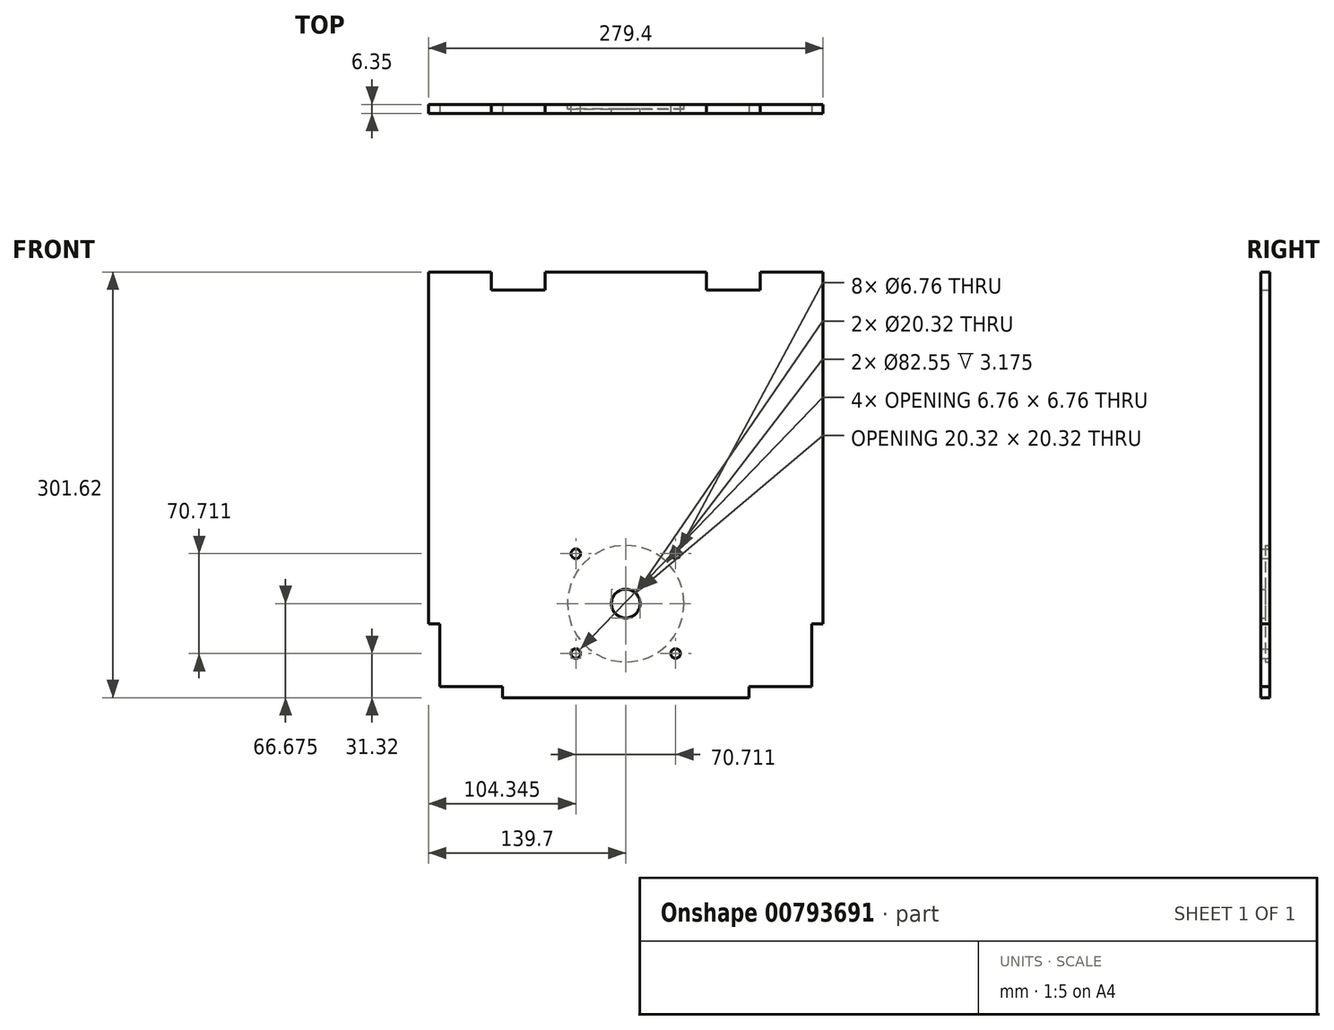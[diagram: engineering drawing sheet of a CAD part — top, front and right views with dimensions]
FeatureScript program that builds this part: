
annotation { "Feature Type Name" : "Feature", "Feature Type Description" : "" }
export const myFeature = defineFeature(function(context is Context, id is Id, definition is map)
    precondition{}
    {
        {
            var Q0;
            Q0=qCreatedBy(makeId("Front.planeOp"),FACE);
            var sketch = newSketch(context, id + "F0", { "sketchPlane" : qUnion([Q0])});
            skLineSegment(sketch, "E0.bottom", {"start": v(0, 0) * mm, "end": v(279.4, 0) * mm});
            skLineSegment(sketch, "E0.top", {"start": v(0, 301.63) * mm, "end": v(44.45, 301.63) * mm});
            skLineSegment(sketch, "E0.left", {"start": v(0, 0) * mm, "end": v(0, 301.63) * mm});
            skLineSegment(sketch, "E0.right", {"start": v(279.4, 0) * mm, "end": v(279.4, 301.63) * mm});
            skLineSegment(sketch, "E1", {"start": v(139.7, 0) * mm, "end": v(139.7, 301.63) * mm, "construction": true});
            skCircle(sketch, "E2", {"center": v(139.7, 66.68) * mm, "radius": 10.16 * mm});
            skCircle(sketch, "E3", {"center": v(139.7, 66.68) * mm, "radius": 50 * mm, "construction": true});
            skLineSegment(sketch, "E4.bottom", {"start": v(184.7, 21.68) * mm, "end": v(94.7, 21.68) * mm, "construction": true});
            skLineSegment(sketch, "E4.top", {"start": v(184.7, 111.67) * mm, "end": v(94.7, 111.67) * mm, "construction": true});
            skLineSegment(sketch, "E4.left", {"start": v(184.7, 21.68) * mm, "end": v(184.7, 111.67) * mm, "construction": true});
            skLineSegment(sketch, "E4.right", {"start": v(94.7, 21.68) * mm, "end": v(94.7, 111.67) * mm, "construction": true});
            skPoint(sketch, "E5", {"position": v(104.34, 31.32) * mm});
            skLineSegment(sketch, "E6", {"start": v(104.34, 31.32) * mm, "end": v(104.34, 21.68) * mm, "construction": true});
            skLineSegment(sketch, "E7", {"start": v(104.34, 31.32) * mm, "end": v(94.7, 31.32) * mm, "construction": true});
            skLineSegment(sketch, "E8", {"start": v(94.7, 66.68) * mm, "end": v(184.7, 66.68) * mm, "construction": true});
            skPoint(sketch, "E9.MirrorP", {"position": v(104.34, 102.03) * mm});
            skPoint(sketch, "E10.MirrorP", {"position": v(175.06, 31.32) * mm});
            skPoint(sketch, "E11.MirrorP", {"position": v(175.06, 102.03) * mm});
            skLineSegment(sketch, "E12.top", {"start": v(234.95, 288.93) * mm, "end": v(196.85, 288.93) * mm});
            skLineSegment(sketch, "E12.left", {"start": v(234.95, 288.93) * mm, "end": v(234.95, 301.63) * mm});
            skLineSegment(sketch, "E12.right", {"start": v(196.85, 288.93) * mm, "end": v(196.85, 301.63) * mm});
            skLineSegment(sketch, "E13.MirrorCS", {"start": v(82.55, 288.93) * mm, "end": v(82.55, 301.63) * mm});
            skLineSegment(sketch, "E14.MirrorCS", {"start": v(44.45, 288.93) * mm, "end": v(82.55, 288.93) * mm});
            skLineSegment(sketch, "E15.MirrorCS", {"start": v(44.45, 288.93) * mm, "end": v(44.45, 301.63) * mm});
            skLineSegment(sketch, "E16.trimOffspring", {"start": v(234.95, 301.63) * mm, "end": v(279.4, 301.63) * mm});
            skPoint(sketch, "E17.MirrorCS.end.orphan", {"position": v(82.55, 301.63) * mm});
            skPoint(sketch, "E17.MirrorCS.start.orphan", {"position": v(44.45, 301.63) * mm});
            skLineSegment(sketch, "E18.trimOffspring", {"start": v(82.55, 301.63) * mm, "end": v(196.85, 301.63) * mm});
            skSolve(sketch);
        }
        {
            var Q0;
            Q0 = qSketchRegion(id + "F0", true);
            extrude(context, id + "F1", {"entities" : qUnion([Q0]), "depth" : 6.35 * mm, "offsetDistance" : 25.4 * mm});
        }
        {
            var Q0;
            Q0=sQuery(id+"F0.wireOp",VERTEX,"E11.MirrorP");
            var Q1;
            Q1=sQuery(id+"F0.wireOp",VERTEX,"E9.MirrorP");
            var Q2;
            Q2=sQuery(id+"F0.wireOp",VERTEX,"E10.MirrorP");
            var Q3;
            Q3=sQuery(id+"F0.wireOp",VERTEX,"E5");
            var Q4;
            Q4=makeQuery(id+"F1.opExtrude","SWEPT_BODY",BODY,{"disambiguationData":[OSD([sQuery(id+"F0.wireOp",EDGE,"E0.bottom"),sQuery(id+"F0.wireOp",EDGE,"E0.top"),sQuery(id+"F0.wireOp",EDGE,"E0.left"),sQuery(id+"F0.wireOp",EDGE,"E0.right"),sQuery(id+"F0.wireOp",EDGE,"E2")])]});
            hole(context, id + "F2", {"style" : HoleStyle.SIMPLE, "endStyle" : HoleEndStyle.THROUGH, "oppositeDirection" : true, "standardTappedOrClearance" : lookupTablePath({ "fit" : "Normal (ASME)", "standard" : "ANSI", "size" : "1/4", "type" : "Clearance" }), "standardBlindInLast" : lookupTablePath({ "fit" : "Free", "standard" : "ANSI", "size" : "1/4", "type" : "Clearance" }), "holeDiameter" : 6.76 * mm, "majorDiameter" : 6.35 * mm, "isTappedThrough" : true, "tappedDepth" : 12.7 * mm, "tapClearance" : 3, "locations" : qUnion([Q0, Q1, Q2, Q3]), "scope" : qUnion([Q4])});
        }
        {
            var Q0;
            Q0=makeQuery(id+"F1.opExtrude","CAP_FACE",FACE,{"disambiguationData":[OSD([sQuery(id+"F0.wireOp",EDGE,"E0.bottom"),sQuery(id+"F0.wireOp",EDGE,"E0.top"),sQuery(id+"F0.wireOp",EDGE,"E0.left"),sQuery(id+"F0.wireOp",EDGE,"E0.right"),sQuery(id+"F0.wireOp",EDGE,"E2")])],"isStart":true});
            var sketch = newSketch(context, id + "F3", { "sketchPlane" : qUnion([Q0])});
            skCircle(sketch, "E19", {"center": v(-139.7, 66.68) * mm, "radius": 41.28 * mm});
            skSolve(sketch);
        }
        {
            var Q0;
            Q0 = qSketchRegion(id + "F3", true);
            extrude(context, id + "F4", {"entities" : qUnion([Q0]), "operationType" : NewBodyOperationType.REMOVE, "oppositeDirection" : true, "depth" : 3.17 * mm, "offsetDistance" : 25.4 * mm});
        }
        {
            var Q0;
            Q0=makeQuery(id+"F1.opExtrude","CAP_FACE",FACE,{"disambiguationData":[OSD([sQuery(id+"F0.wireOp",EDGE,"E0.bottom"),sQuery(id+"F0.wireOp",EDGE,"E0.top"),sQuery(id+"F0.wireOp",EDGE,"E0.left"),sQuery(id+"F0.wireOp",EDGE,"E0.right"),sQuery(id+"F0.wireOp",EDGE,"E2"),sQuery(id+"F0.wireOp",EDGE,"E12.top"),sQuery(id+"F0.wireOp",EDGE,"E12.left"),sQuery(id+"F0.wireOp",EDGE,"E12.right"),sQuery(id+"F0.wireOp",EDGE,"E13.MirrorCS"),sQuery(id+"F0.wireOp",EDGE,"E14.MirrorCS"),sQuery(id+"F0.wireOp",EDGE,"E15.MirrorCS"),sQuery(id+"F0.wireOp",EDGE,"E16.trimOffspring"),sQuery(id+"F0.wireOp",EDGE,"E18.trimOffspring")])],"isStart":false});
            var sketch = newSketch(context, id + "F5", { "sketchPlane" : qUnion([Q0])});
            skLineSegment(sketch, "E20", {"start": v(139.7, 301.63) * mm, "end": v(139.7, 0) * mm, "construction": true});
            skLineSegment(sketch, "E21", {"start": v(52.39, 0) * mm, "end": v(52.39, 7.94) * mm});
            skLineSegment(sketch, "E22", {"start": v(52.39, 7.94) * mm, "end": v(7.94, 7.94) * mm});
            skLineSegment(sketch, "E23", {"start": v(7.94, 7.94) * mm, "end": v(7.94, 52.39) * mm});
            skLineSegment(sketch, "E24", {"start": v(7.94, 52.39) * mm, "end": v(0, 52.39) * mm});
            skLineSegment(sketch, "E25.MirrorCS", {"start": v(227.01, 0) * mm, "end": v(227.01, 7.94) * mm});
            skLineSegment(sketch, "E26.MirrorCS", {"start": v(227.01, 7.94) * mm, "end": v(271.46, 7.94) * mm});
            skLineSegment(sketch, "E27.MirrorCS", {"start": v(271.46, 7.94) * mm, "end": v(271.46, 52.39) * mm});
            skLineSegment(sketch, "E28.MirrorCS", {"start": v(271.46, 52.39) * mm, "end": v(279.4, 52.39) * mm});
            skSolve(sketch);
        }
        {
            var Q0;
            {var subQ4=sQuery(id+"F5.wireOp",EDGE,"E25.MirrorCS");Q0=makeQuery(id+"F5.imprint","IMPRINT",FACE,{"disambiguationData":[TD([[makeQuery(id+"F5.imprint","IMPRINT",EDGE,{"derivedFrom":subQ4}),-1.0]])]});}
            var Q1;
            {var subQ4=sQuery(id+"F5.wireOp",EDGE,"E21");Q1=makeQuery(id+"F5.imprint","IMPRINT",FACE,{"disambiguationData":[TD([[makeQuery(id+"F5.imprint","IMPRINT",EDGE,{"derivedFrom":subQ4}),1.0]])]});}
            extrude(context, id + "F6", {"entities" : qUnion([Q0, Q1]), "operationType" : NewBodyOperationType.REMOVE, "oppositeDirection" : true, "depth" : 25.4 * mm, "offsetDistance" : 25.4 * mm});
        }
        {
            var Q0;
            Q0=makeQuery(id+"F1.opExtrude","SWEPT_BODY",BODY,{"disambiguationData":[OSD([sQuery(id+"F0.wireOp",EDGE,"E0.bottom"),sQuery(id+"F0.wireOp",EDGE,"E0.top"),sQuery(id+"F0.wireOp",EDGE,"E0.left"),sQuery(id+"F0.wireOp",EDGE,"E0.right"),sQuery(id+"F0.wireOp",EDGE,"E2"),sQuery(id+"F0.wireOp",EDGE,"E12.top"),sQuery(id+"F0.wireOp",EDGE,"E12.left"),sQuery(id+"F0.wireOp",EDGE,"E12.right"),sQuery(id+"F0.wireOp",EDGE,"E13.MirrorCS"),sQuery(id+"F0.wireOp",EDGE,"E14.MirrorCS"),sQuery(id+"F0.wireOp",EDGE,"E15.MirrorCS"),sQuery(id+"F0.wireOp",EDGE,"E16.trimOffspring"),sQuery(id+"F0.wireOp",EDGE,"E18.trimOffspring")])]});
            transform(context, id + "F7", {"entities" : qUnion([Q0]), "transformType" : TransformType.TRANSLATION_3D, "dx" : 0 * mm, "dy" : 0 * mm, "dz" : 0 * mm, "makeCopy" : true});
        }
    });
